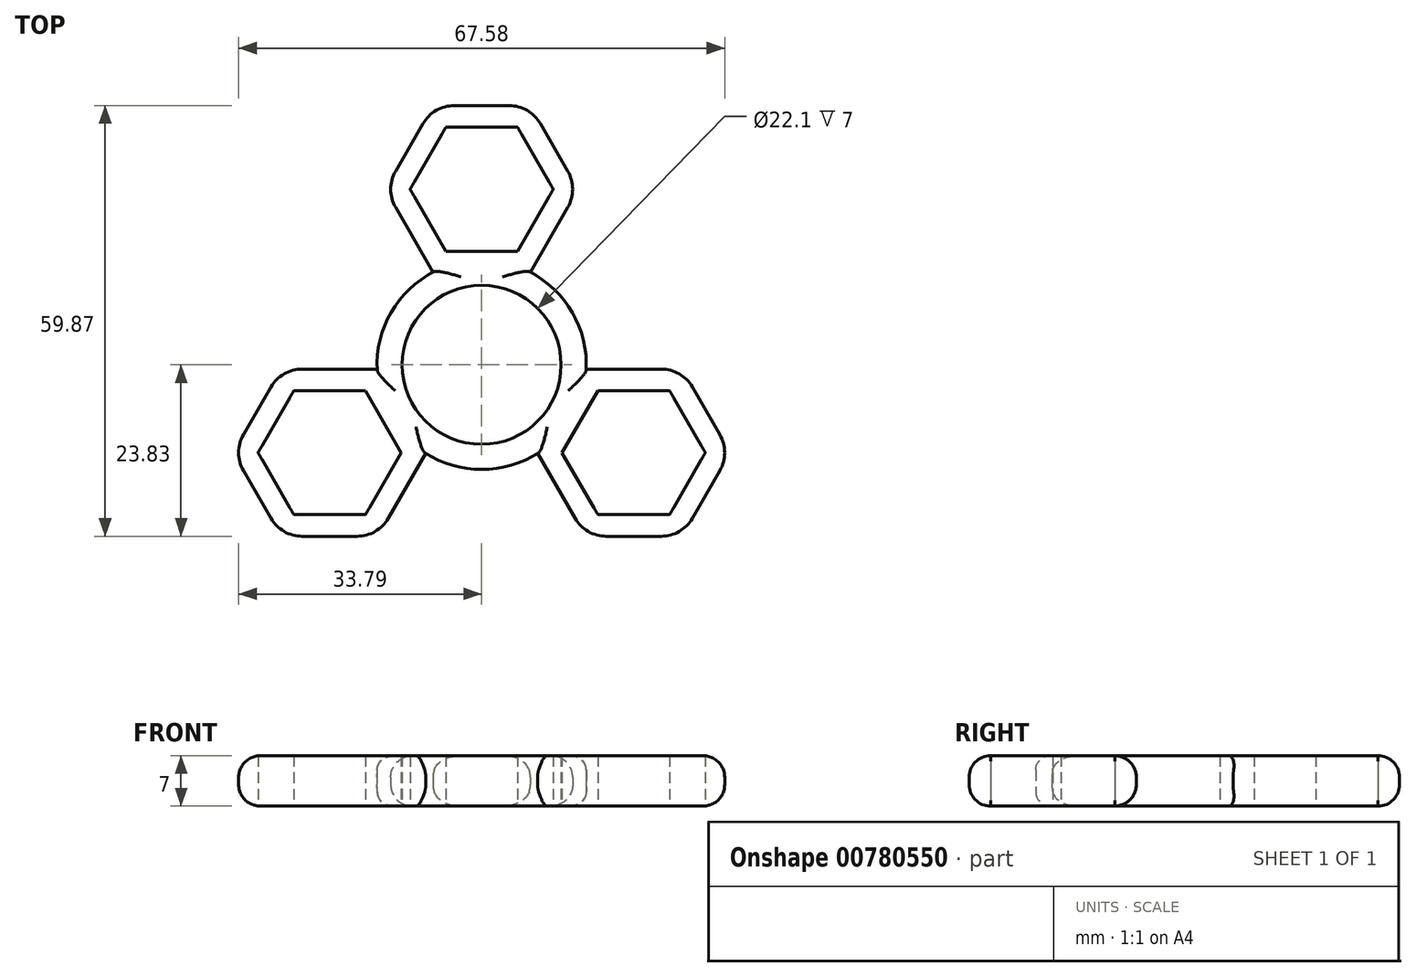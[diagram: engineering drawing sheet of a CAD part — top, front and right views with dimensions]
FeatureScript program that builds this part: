
annotation { "Feature Type Name" : "Feature", "Feature Type Description" : "" }
export const myFeature = defineFeature(function(context is Context, id is Id, definition is map)
    precondition{}
    {
        {
            var Q0;
            Q0=qCreatedBy(makeId("Top.planeOp"),FACE);
            var sketch = newSketch(context, id + "F0", { "sketchPlane" : qUnion([Q0])});
            skCircle(sketch, "E0", {"center": v(0, 0) * mm, "radius": 11.05 * mm});
            skCircle(sketch, "E1.0", {"center": v(0, 0) * mm, "radius": 14.55 * mm});
            skCircle(sketch, "E2.cCircle", {"center": v(0, 0) * mm, "radius": 19.75 * mm, "construction": true});
            skCircle(sketch, "E3.cCircle", {"center": v(0, 24.41) * mm, "radius": 8.62 * mm, "construction": true});
            skLineSegment(sketch, "E3.0", {"start": v(-4.98, 33.04) * mm, "end": v(4.98, 33.04) * mm});
            skLineSegment(sketch, "E3.1", {"start": v(4.98, 33.04) * mm, "end": v(9.96, 24.41) * mm});
            skLineSegment(sketch, "E3.2", {"start": v(9.96, 24.41) * mm, "end": v(4.98, 15.79) * mm});
            skLineSegment(sketch, "E3.3", {"start": v(4.98, 15.79) * mm, "end": v(-4.98, 15.79) * mm});
            skLineSegment(sketch, "E3.4", {"start": v(-4.98, 15.79) * mm, "end": v(-9.96, 24.41) * mm});
            skLineSegment(sketch, "E3.5", {"start": v(-9.96, 24.41) * mm, "end": v(-4.98, 33.04) * mm});
            skPoint(sketch, "E3.0.midPoint", {"position": v(0, 33.04) * mm});
            skLineSegment(sketch, "E4.0", {"start": v(-13.42, 24.41) * mm, "end": v(-6.71, 36.04) * mm});
            skLineSegment(sketch, "E4.1", {"start": v(6.71, 36.04) * mm, "end": v(13.42, 24.41) * mm});
            skLineSegment(sketch, "E4.2", {"start": v(13.42, 24.41) * mm, "end": v(6.71, 12.79) * mm});
            skLineSegment(sketch, "E4.3", {"start": v(-6.71, 36.04) * mm, "end": v(6.71, 36.04) * mm});
            skLineSegment(sketch, "E4.4", {"start": v(6.71, 12.79) * mm, "end": v(-6.71, 12.79) * mm});
            skLineSegment(sketch, "E4.5", {"start": v(-6.71, 12.79) * mm, "end": v(-13.42, 24.41) * mm});
            skSolve(sketch);
        }
        {
            var Q0;
            Q0=qSketchRegion(id+"F0",true);
            extrude(context, id + "F1", {"entities" : qUnion([Q0]), "depth" : 7 * mm, "offsetDistance" : 25 * mm});
        }
        {
            var Q0;
            Q0=makeQuery(id+"F1.opExtrude","SWEPT_EDGE",EDGE,{"disambiguationData":[OSD([sQuery(id+"F0.wireOp",EDGE,"e8ea1e39-c8e4-4f1f-8f41-e8bb20e3dc64.0"),sQuery(id+"F0.wireOp",EDGE,"e8ea1e39-c8e4-4f1f-8f41-e8bb20e3dc64.5")])]});
            var Q1;
            Q1=makeQuery(id+"F1.opExtrude","SWEPT_EDGE",EDGE,{"disambiguationData":[OSD([sQuery(id+"F0.wireOp",EDGE,"e8ea1e39-c8e4-4f1f-8f41-e8bb20e3dc64.2"),sQuery(id+"F0.wireOp",EDGE,"e8ea1e39-c8e4-4f1f-8f41-e8bb20e3dc64.4")])]});
            var Q2;
            Q2=makeQuery(id+"F1.opExtrude","SWEPT_EDGE",EDGE,{"disambiguationData":[OSD([sQuery(id+"F0.wireOp",EDGE,"e8ea1e39-c8e4-4f1f-8f41-e8bb20e3dc64.1"),sQuery(id+"F0.wireOp",EDGE,"e8ea1e39-c8e4-4f1f-8f41-e8bb20e3dc64.2")])]});
            var Q3;
            Q3=makeQuery(id+"F1.opExtrude","SWEPT_EDGE",EDGE,{"disambiguationData":[OSD([sQuery(id+"F0.wireOp",EDGE,"bc2e01c2-815f-4e23-ab08-36e09104f585.2"),sQuery(id+"F0.wireOp",EDGE,"bc2e01c2-815f-4e23-ab08-36e09104f585.4")])]});
            var Q4;
            Q4=makeQuery(id+"F1.opExtrude","SWEPT_EDGE",EDGE,{"disambiguationData":[OSD([sQuery(id+"F0.wireOp",EDGE,"bc2e01c2-815f-4e23-ab08-36e09104f585.1"),sQuery(id+"F0.wireOp",EDGE,"bc2e01c2-815f-4e23-ab08-36e09104f585.2")])]});
            var Q5;
            Q5=makeQuery(id+"F1.opExtrude","SWEPT_EDGE",EDGE,{"disambiguationData":[OSD([sQuery(id+"F0.wireOp",EDGE,"bc2e01c2-815f-4e23-ab08-36e09104f585.1"),sQuery(id+"F0.wireOp",EDGE,"bc2e01c2-815f-4e23-ab08-36e09104f585.3")])]});
            var Q6;
            Q6=makeQuery(id+"F1.opExtrude","SWEPT_EDGE",EDGE,{"disambiguationData":[OSD([sQuery(id+"F0.wireOp",EDGE,"bc2e01c2-815f-4e23-ab08-36e09104f585.0"),sQuery(id+"F0.wireOp",EDGE,"bc2e01c2-815f-4e23-ab08-36e09104f585.3")])]});
            var Q7;
            Q7=makeQuery(id+"F1.opExtrude","SWEPT_EDGE",EDGE,{"disambiguationData":[OSD([sQuery(id+"F0.wireOp",EDGE,"E4.1"),sQuery(id+"F0.wireOp",EDGE,"E4.2")])]});
            var Q8;
            Q8=makeQuery(id+"F1.opExtrude","SWEPT_EDGE",EDGE,{"disambiguationData":[OSD([sQuery(id+"F0.wireOp",EDGE,"E4.1"),sQuery(id+"F0.wireOp",EDGE,"E4.3")])]});
            var Q9;
            Q9=makeQuery(id+"F1.opExtrude","SWEPT_EDGE",EDGE,{"disambiguationData":[OSD([sQuery(id+"F0.wireOp",EDGE,"E4.0"),sQuery(id+"F0.wireOp",EDGE,"E4.3")])]});
            var Q10;
            Q10=makeQuery(id+"F1.opExtrude","SWEPT_EDGE",EDGE,{"disambiguationData":[OSD([sQuery(id+"F0.wireOp",EDGE,"E4.0"),sQuery(id+"F0.wireOp",EDGE,"E4.5")])]});
            var Q11;
            Q11=makeQuery(id+"F1.opExtrude","SWEPT_EDGE",EDGE,{"disambiguationData":[OSD([sQuery(id+"F0.wireOp",EDGE,"88b40c85-247c-4d13-ac2e-2eb34554f8ad.1"),sQuery(id+"F0.wireOp",EDGE,"88b40c85-247c-4d13-ac2e-2eb34554f8ad.3")])]});
            var Q12;
            Q12=makeQuery(id+"F1.opExtrude","SWEPT_EDGE",EDGE,{"disambiguationData":[OSD([sQuery(id+"F0.wireOp",EDGE,"88b40c85-247c-4d13-ac2e-2eb34554f8ad.0"),sQuery(id+"F0.wireOp",EDGE,"88b40c85-247c-4d13-ac2e-2eb34554f8ad.3")])]});
            var Q13;
            Q13=makeQuery(id+"F1.opExtrude","SWEPT_EDGE",EDGE,{"disambiguationData":[OSD([sQuery(id+"F0.wireOp",EDGE,"88b40c85-247c-4d13-ac2e-2eb34554f8ad.0"),sQuery(id+"F0.wireOp",EDGE,"88b40c85-247c-4d13-ac2e-2eb34554f8ad.5")])]});
            var Q14;
            Q14=makeQuery(id+"F1.opExtrude","SWEPT_EDGE",EDGE,{"disambiguationData":[OSD([sQuery(id+"F0.wireOp",EDGE,"88b40c85-247c-4d13-ac2e-2eb34554f8ad.4"),sQuery(id+"F0.wireOp",EDGE,"88b40c85-247c-4d13-ac2e-2eb34554f8ad.5")])]});
            var Q15;
            Q15=makeQuery(id+"F1.opExtrude","SWEPT_EDGE",EDGE,{"disambiguationData":[OSD([sQuery(id+"F0.wireOp",EDGE,"e039e999-560e-4138-92c9-75450f4679a6.0"),sQuery(id+"F0.wireOp",EDGE,"e039e999-560e-4138-92c9-75450f4679a6.3")])]});
            var Q16;
            Q16=makeQuery(id+"F1.opExtrude","SWEPT_EDGE",EDGE,{"disambiguationData":[OSD([sQuery(id+"F0.wireOp",EDGE,"e039e999-560e-4138-92c9-75450f4679a6.0"),sQuery(id+"F0.wireOp",EDGE,"e039e999-560e-4138-92c9-75450f4679a6.5")])]});
            var Q17;
            Q17=makeQuery(id+"F1.opExtrude","SWEPT_EDGE",EDGE,{"disambiguationData":[OSD([sQuery(id+"F0.wireOp",EDGE,"e039e999-560e-4138-92c9-75450f4679a6.4"),sQuery(id+"F0.wireOp",EDGE,"e039e999-560e-4138-92c9-75450f4679a6.5")])]});
            var Q18;
            Q18=makeQuery(id+"F1.opExtrude","SWEPT_EDGE",EDGE,{"disambiguationData":[OSD([sQuery(id+"F0.wireOp",EDGE,"e039e999-560e-4138-92c9-75450f4679a6.2"),sQuery(id+"F0.wireOp",EDGE,"e039e999-560e-4138-92c9-75450f4679a6.4")])]});
            var Q19;
            Q19=makeQuery(id+"F1.opExtrude","SWEPT_EDGE",EDGE,{"disambiguationData":[OSD([sQuery(id+"F0.wireOp",EDGE,"e8ea1e39-c8e4-4f1f-8f41-e8bb20e3dc64.4"),sQuery(id+"F0.wireOp",EDGE,"e8ea1e39-c8e4-4f1f-8f41-e8bb20e3dc64.5")])]});
            fillet(context, id + "F2", {"entities" : qUnion([Q0, Q1, Q2, Q3, Q4, Q5, Q6, Q7, Q8, Q9, Q10, Q11, Q12, Q13, Q14, Q15, Q16, Q17, Q18, Q19]), "radius" : 5 * mm, "tangentPropagation" : true, "allowEdgeOverflow" : false});
        }
        {
            var Q0;
            Q0=makeQuery(id+"F1.opExtrude","CAP_EDGE",EDGE,{"disambiguationData":[OSD([sQuery(id+"F0.wireOp",EDGE,"e039e999-560e-4138-92c9-75450f4679a6.4")])],"isStart":true});
            var Q1;
            Q1=makeQuery(id+"F1.opExtrude","CAP_EDGE",EDGE,{"disambiguationData":[OSD([sQuery(id+"F0.wireOp",EDGE,"e8ea1e39-c8e4-4f1f-8f41-e8bb20e3dc64.5")])],"isStart":true});
            var Q2;
            Q2=makeQuery(id+"F1.opExtrude","CAP_EDGE",EDGE,{"disambiguationData":[OSD([sQuery(id+"F0.wireOp",EDGE,"bc2e01c2-815f-4e23-ab08-36e09104f585.2")])],"isStart":true});
            var Q3;
            Q3=makeQuery(id+"F1.opExtrude","CAP_EDGE",EDGE,{"disambiguationData":[OSD([sQuery(id+"F0.wireOp",EDGE,"E4.2")])],"isStart":true});
            var Q4;
            Q4=makeQuery(id+"F1.opExtrude","CAP_EDGE",EDGE,{"disambiguationData":[OSD([sQuery(id+"F0.wireOp",EDGE,"88b40c85-247c-4d13-ac2e-2eb34554f8ad.3")])],"isStart":true});
            var Q5;
            Q5=makeQuery(id+"F1.opExtrude","CAP_EDGE",EDGE,{"disambiguationData":[OSD([sQuery(id+"F0.wireOp",EDGE,"bc2e01c2-815f-4e23-ab08-36e09104f585.1")])],"isStart":false});
            var Q6;
            Q6=makeQuery(id+"F1.opExtrude","CAP_EDGE",EDGE,{"disambiguationData":[OSD([sQuery(id+"F0.wireOp",EDGE,"e8ea1e39-c8e4-4f1f-8f41-e8bb20e3dc64.2")])],"isStart":false});
            var Q7;
            Q7=makeQuery(id+"F1.opExtrude","CAP_EDGE",EDGE,{"disambiguationData":[OSD([sQuery(id+"F0.wireOp",EDGE,"e039e999-560e-4138-92c9-75450f4679a6.5")])],"isStart":false});
            var Q8;
            Q8=makeQuery(id+"F1.opExtrude","CAP_EDGE",EDGE,{"disambiguationData":[OSD([sQuery(id+"F0.wireOp",EDGE,"88b40c85-247c-4d13-ac2e-2eb34554f8ad.5")])],"isStart":false});
            var Q9;
            Q9=makeQuery(id+"F1.opExtrude","CAP_EDGE",EDGE,{"disambiguationData":[OSD([sQuery(id+"F0.wireOp",EDGE,"E4.0")])],"isStart":false});
            fillet(context, id + "F3", {"entities" : qUnion([Q0, Q1, Q2, Q3, Q4, Q5, Q6, Q7, Q8, Q9]), "radius" : 3 * mm, "tangentPropagation" : true, "allowEdgeOverflow" : false});
        }
        {
            var Q0;
            {var subQ0=sQuery(id+"F0.wireOp",EDGE,"E1.0");Q0=makeQuery(id+"F1.opExtrude","CAP_EDGE",EDGE,{"disambiguationData":[OSD([subQ0]),TDD([makeQuery(id+"F0.imprint","IMPRINT",EDGE,{"disambiguationData":[TD([[makeQuery(id+"F0.imprint","INTERSECT",VERTEX,{"derivedFrom":[subQ0,sQuery(id+"F0.wireOp",EDGE,"e039e999-560e-4138-92c9-75450f4679a6.2")]}),-1.0]])],"derivedFrom":subQ0})])],"isStart":false});}
            var Q1;
            {var subQ0=sQuery(id+"F0.wireOp",EDGE,"E1.0");Q1=makeQuery(id+"F1.opExtrude","CAP_EDGE",EDGE,{"disambiguationData":[OSD([subQ0]),TDD([makeQuery(id+"F0.imprint","IMPRINT",EDGE,{"disambiguationData":[TD([[makeQuery(id+"F0.imprint","INTERSECT",VERTEX,{"derivedFrom":[subQ0,sQuery(id+"F0.wireOp",EDGE,"e8ea1e39-c8e4-4f1f-8f41-e8bb20e3dc64.1")]}),-1.0]])],"derivedFrom":subQ0})])],"isStart":false});}
            var Q2;
            {var subQ0=sQuery(id+"F0.wireOp",EDGE,"E1.0");Q2=makeQuery(id+"F1.opExtrude","CAP_EDGE",EDGE,{"disambiguationData":[OSD([subQ0]),TDD([makeQuery(id+"F0.imprint","IMPRINT",EDGE,{"disambiguationData":[TD([[makeQuery(id+"F0.imprint","INTERSECT",VERTEX,{"derivedFrom":[subQ0,sQuery(id+"F0.wireOp",EDGE,"E4.2")]}),1.0]])],"derivedFrom":subQ0})])],"isStart":false});}
            var Q3;
            {var subQ0=sQuery(id+"F0.wireOp",EDGE,"E1.0");Q3=makeQuery(id+"F1.opExtrude","CAP_EDGE",EDGE,{"disambiguationData":[OSD([subQ0]),TDD([makeQuery(id+"F0.imprint","IMPRINT",EDGE,{"disambiguationData":[TD([[makeQuery(id+"F0.imprint","INTERSECT",VERTEX,{"derivedFrom":[subQ0,sQuery(id+"F0.wireOp",EDGE,"E4.5")]}),-1.0]])],"derivedFrom":subQ0})])],"isStart":false});}
            var Q4;
            {var subQ0=sQuery(id+"F0.wireOp",EDGE,"E1.0");Q4=makeQuery(id+"F1.opExtrude","CAP_EDGE",EDGE,{"disambiguationData":[OSD([subQ0]),TDD([makeQuery(id+"F0.imprint","IMPRINT",EDGE,{"disambiguationData":[TD([[makeQuery(id+"F0.imprint","INTERSECT",VERTEX,{"derivedFrom":[subQ0,sQuery(id+"F0.wireOp",EDGE,"88b40c85-247c-4d13-ac2e-2eb34554f8ad.4")]}),-1.0]])],"derivedFrom":subQ0})])],"isStart":false});}
            var Q5;
            {var subQ0=sQuery(id+"F0.wireOp",EDGE,"E1.0");Q5=makeQuery(id+"F1.opExtrude","CAP_EDGE",EDGE,{"disambiguationData":[OSD([subQ0]),TDD([makeQuery(id+"F0.imprint","IMPRINT",EDGE,{"disambiguationData":[TD([[makeQuery(id+"F0.imprint","INTERSECT",VERTEX,{"derivedFrom":[subQ0,sQuery(id+"F0.wireOp",EDGE,"e039e999-560e-4138-92c9-75450f4679a6.2")]}),-1.0]])],"derivedFrom":subQ0})])],"isStart":true});}
            var Q6;
            {var subQ0=sQuery(id+"F0.wireOp",EDGE,"E1.0");Q6=makeQuery(id+"F1.opExtrude","CAP_EDGE",EDGE,{"disambiguationData":[OSD([subQ0]),TDD([makeQuery(id+"F0.imprint","IMPRINT",EDGE,{"disambiguationData":[TD([[makeQuery(id+"F0.imprint","INTERSECT",VERTEX,{"derivedFrom":[subQ0,sQuery(id+"F0.wireOp",EDGE,"e8ea1e39-c8e4-4f1f-8f41-e8bb20e3dc64.1")]}),-1.0]])],"derivedFrom":subQ0})])],"isStart":true});}
            var Q7;
            {var subQ0=sQuery(id+"F0.wireOp",EDGE,"E1.0");Q7=makeQuery(id+"F1.opExtrude","CAP_EDGE",EDGE,{"disambiguationData":[OSD([subQ0]),TDD([makeQuery(id+"F0.imprint","IMPRINT",EDGE,{"disambiguationData":[TD([[makeQuery(id+"F0.imprint","INTERSECT",VERTEX,{"derivedFrom":[subQ0,sQuery(id+"F0.wireOp",EDGE,"E4.2")]}),1.0]])],"derivedFrom":subQ0})])],"isStart":true});}
            var Q8;
            {var subQ0=sQuery(id+"F0.wireOp",EDGE,"E1.0");Q8=makeQuery(id+"F1.opExtrude","CAP_EDGE",EDGE,{"disambiguationData":[OSD([subQ0]),TDD([makeQuery(id+"F0.imprint","IMPRINT",EDGE,{"disambiguationData":[TD([[makeQuery(id+"F0.imprint","INTERSECT",VERTEX,{"derivedFrom":[subQ0,sQuery(id+"F0.wireOp",EDGE,"E4.5")]}),-1.0]])],"derivedFrom":subQ0})])],"isStart":true});}
            var Q9;
            {var subQ0=sQuery(id+"F0.wireOp",EDGE,"E1.0");Q9=makeQuery(id+"F1.opExtrude","CAP_EDGE",EDGE,{"disambiguationData":[OSD([subQ0]),TDD([makeQuery(id+"F0.imprint","IMPRINT",EDGE,{"disambiguationData":[TD([[makeQuery(id+"F0.imprint","INTERSECT",VERTEX,{"derivedFrom":[subQ0,sQuery(id+"F0.wireOp",EDGE,"88b40c85-247c-4d13-ac2e-2eb34554f8ad.4")]}),-1.0]])],"derivedFrom":subQ0})])],"isStart":true});}
            fillet(context, id + "F4", {"entities" : qUnion([Q0, Q1, Q2, Q3, Q4, Q5, Q6, Q7, Q8, Q9]), "radius" : 2 * mm, "tangentPropagation" : true, "allowEdgeOverflow" : false});
        }
        {
            var Q0;
            Q0=makeQuery(id+"F1.opExtrude","SWEPT_BODY",BODY,{"disambiguationData":[OSD([sQuery(id+"F0.wireOp",EDGE,"E0"),sQuery(id+"F0.wireOp",EDGE,"E1.0"),sQuery(id+"F0.wireOp",EDGE,"E3.0"),sQuery(id+"F0.wireOp",EDGE,"E3.1"),sQuery(id+"F0.wireOp",EDGE,"E3.2"),sQuery(id+"F0.wireOp",EDGE,"E3.3"),sQuery(id+"F0.wireOp",EDGE,"E3.4"),sQuery(id+"F0.wireOp",EDGE,"E3.5"),sQuery(id+"F0.wireOp",EDGE,"E4.0"),sQuery(id+"F0.wireOp",EDGE,"E4.1"),sQuery(id+"F0.wireOp",EDGE,"E4.2"),sQuery(id+"F0.wireOp",EDGE,"E4.3"),sQuery(id+"F0.wireOp",EDGE,"E4.5")])]});
            var Q1;
            Q1=makeQuery(id+"F1.opExtrude","SWEPT_FACE",FACE,{"disambiguationData":[OSD([sQuery(id+"F0.wireOp",EDGE,"E0")])]});
            circularPattern(context, id + "F5", {"operationType" : NewBodyOperationType.ADD, "entities" : qUnion([Q0]), "axis" : qUnion([Q1]), "angle" : 360 * degree, "instanceCount" : 3, "equalSpace" : true});
        }
    });
